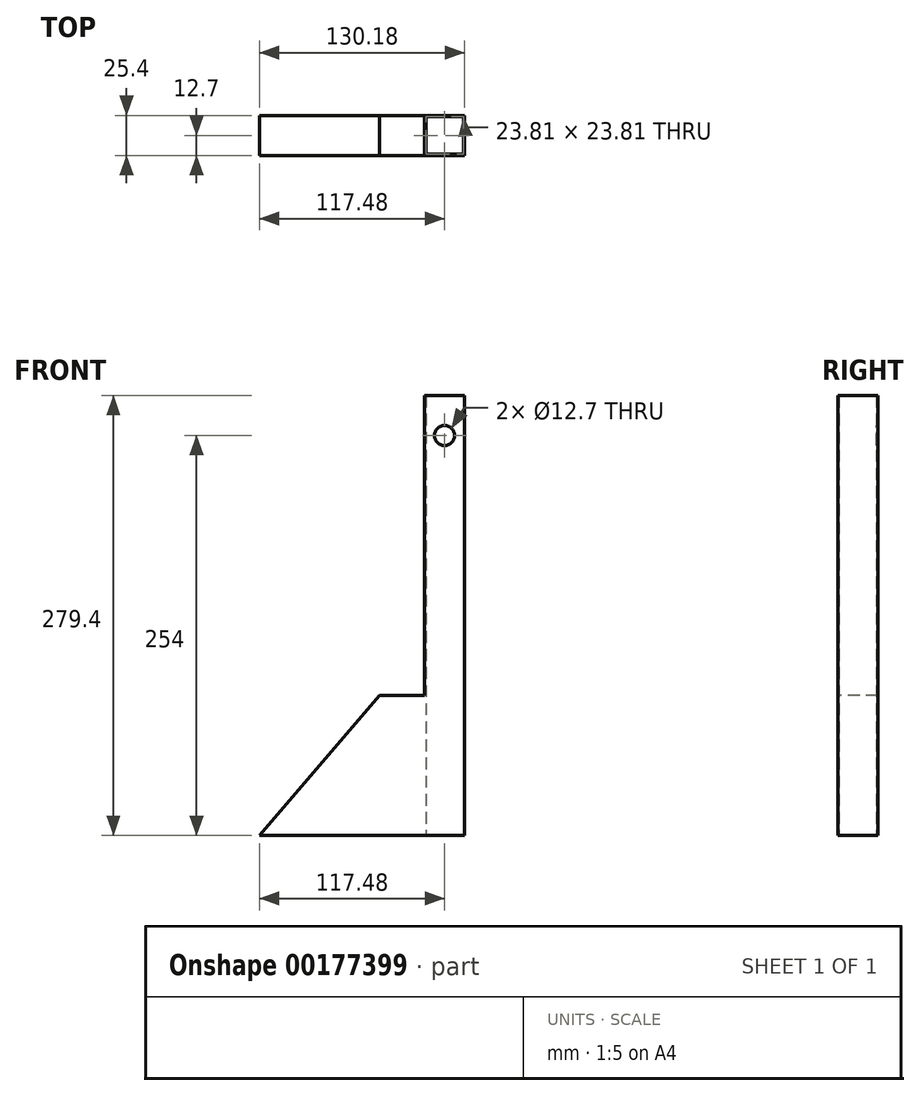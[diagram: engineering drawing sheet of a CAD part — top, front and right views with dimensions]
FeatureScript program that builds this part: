
annotation { "Feature Type Name" : "Feature", "Feature Type Description" : "" }
export const myFeature = defineFeature(function(context is Context, id is Id, definition is map)
    precondition{}
    {
        {
            var Q0;
            Q0=qCreatedBy(makeId("Top.planeOp"),FACE);
            var sketch = newSketch(context, id + "F0", { "sketchPlane" : qUnion([Q0])});
            skLineSegment(sketch, "E0.bottom", {"start": v(12.7, -12.7) * mm, "end": v(-12.7, -12.7) * mm});
            skLineSegment(sketch, "E0.top", {"start": v(12.7, 12.7) * mm, "end": v(-12.7, 12.7) * mm});
            skLineSegment(sketch, "E0.left", {"start": v(12.7, -12.7) * mm, "end": v(12.7, 12.7) * mm});
            skLineSegment(sketch, "E0.right", {"start": v(-12.7, -12.7) * mm, "end": v(-12.7, 12.7) * mm});
            skPoint(sketch, "E0.middle", {"position": v(0, 0) * mm});
            skLineSegment(sketch, "E1.bottom", {"start": v(11.9, -11.9) * mm, "end": v(-11.9, -11.9) * mm});
            skLineSegment(sketch, "E1.top", {"start": v(11.9, 11.9) * mm, "end": v(-11.9, 11.9) * mm});
            skLineSegment(sketch, "E1.left", {"start": v(11.9, -11.9) * mm, "end": v(11.9, 11.9) * mm});
            skLineSegment(sketch, "E1.right", {"start": v(-11.9, -11.9) * mm, "end": v(-11.9, 11.9) * mm});
            skSolve(sketch);
        }
        {
            var Q0;
            Q0=makeQuery(id+"F0.imprint","IMPRINT",FACE,{"disambiguationData":[TD([[makeQuery(id+"F0.imprint","IMPRINT",EDGE,{"derivedFrom":sQuery(id+"F0.wireOp",EDGE,"E0.bottom")}),-1.0]])]});
            extrude(context, id + "F1", {"entities" : qUnion([Q0]), "depth" : 279.4 * mm});
        }
        {
            var Q0;
            Q0=makeQuery(id+"F1.opExtrude","SWEPT_FACE",FACE,{"disambiguationData":[OSD([sQuery(id+"F0.wireOp",EDGE,"E0.bottom")])]});
            var sketch = newSketch(context, id + "F2", { "sketchPlane" : qUnion([Q0])});
            skLineSegment(sketch, "E2.MirrorCS", {"start": v(-12.7, 0) * mm, "end": v(-12.7, 88.9) * mm});
            skLineSegment(sketch, "E3.MirrorCS", {"start": v(-12.7, 88.9) * mm, "end": v(-41.28, 88.9) * mm});
            skLineSegment(sketch, "E4.MirrorCS", {"start": v(-41.27, 88.9) * mm, "end": v(-117.48, 0) * mm});
            skLineSegment(sketch, "E5.MirrorCS", {"start": v(-12.7, 0) * mm, "end": v(-117.48, 0) * mm});
            skSolve(sketch);
        }
        {
            var Q0;
            Q0=makeQuery(id+"F2.imprint","IMPRINT",FACE,{"disambiguationData":[TD([[makeQuery(id+"F2.imprint","IMPRINT",EDGE,{"derivedFrom":sQuery(id+"F2.wireOp",EDGE,"E2.MirrorCS")}),-1.0]])]});
            extrude(context, id + "F3", {"entities" : qUnion([Q0]), "oppositeDirection" : true, "depth" : 25.4 * mm});
        }
        {
            var Q0;
            Q0=makeQuery(id+"F1.opExtrude","SWEPT_BODY",BODY,{"disambiguationData":[OSD([sQuery(id+"F0.wireOp",EDGE,"E0.bottom"),sQuery(id+"F0.wireOp",EDGE,"E0.top"),sQuery(id+"F0.wireOp",EDGE,"E0.left"),sQuery(id+"F0.wireOp",EDGE,"E0.right"),sQuery(id+"F0.wireOp",EDGE,"E1.bottom"),sQuery(id+"F0.wireOp",EDGE,"E1.top"),sQuery(id+"F0.wireOp",EDGE,"E1.left"),sQuery(id+"F0.wireOp",EDGE,"E1.right")])]});
            var Q1;
            Q1=makeQuery(id+"F3.opExtrude","SWEPT_BODY",BODY,{"disambiguationData":[OSD([sQuery(id+"F2.wireOp",EDGE,"E2.MirrorCS"),sQuery(id+"F2.wireOp",EDGE,"E3.MirrorCS"),sQuery(id+"F2.wireOp",EDGE,"E4.MirrorCS"),sQuery(id+"F2.wireOp",EDGE,"E5.MirrorCS")])]});
            booleanBodies(context, id + "F4", {"operationType" : BooleanOperationType.UNION, "tools" : qUnion([Q0, Q1])});
        }
        {
            var Q0;
            Q0=makeQuery(id+"F4.opBoolean","MERGE",FACE,{"derivedFrom":[makeQuery(id+"F1.opExtrude","SWEPT_FACE",FACE,{"disambiguationData":[OSD([sQuery(id+"F0.wireOp",EDGE,"E0.bottom")])]}),makeQuery(id+"F3.opExtrude","CAP_FACE",FACE,{"disambiguationData":[OSD([sQuery(id+"F2.wireOp",EDGE,"1QGrf0qa-TmRB-KGXR-dZYk-SKFY90kVTzdY"),sQuery(id+"F2.wireOp",EDGE,"2tY0wfcE-ghAz-ktQM-IzCy-QUitCEAG6IOc"),sQuery(id+"F2.wireOp",EDGE,"oejEbDKt-iHby-fXsX-wvyz-NOz1VG9v0LQn"),sQuery(id+"F2.wireOp",EDGE,"JJ2piEfX-4vLk-RoDB-PwuK-YiFWx0NtQUjr")])],"isStart":true})]});
            var sketch = newSketch(context, id + "F5", { "sketchPlane" : qUnion([Q0])});
            skLineSegment(sketch, "E6", {"start": v(0, 279.4) * mm, "end": v(0, 254) * mm});
            skPoint(sketch, "E6.endSnap0", {"position": v(0, 279.4) * mm});
            skCircle(sketch, "E7", {"center": v(0, 254) * mm, "radius": 6.35 * mm});
            skSolve(sketch);
        }
        {
            var Q0;
            Q0=makeQuery(id+"F5.imprint","IMPRINT",FACE,{"disambiguationData":[TD([[makeQuery(id+"F5.imprint","IMPRINT",EDGE,{"derivedFrom":sQuery(id+"F5.wireOp",EDGE,"E7")}),1.0]])]});
            extrude(context, id + "F6", {"entities" : qUnion([Q0]), "operationType" : NewBodyOperationType.REMOVE, "oppositeDirection" : true, "depth" : 25.4 * mm});
        }
    });
